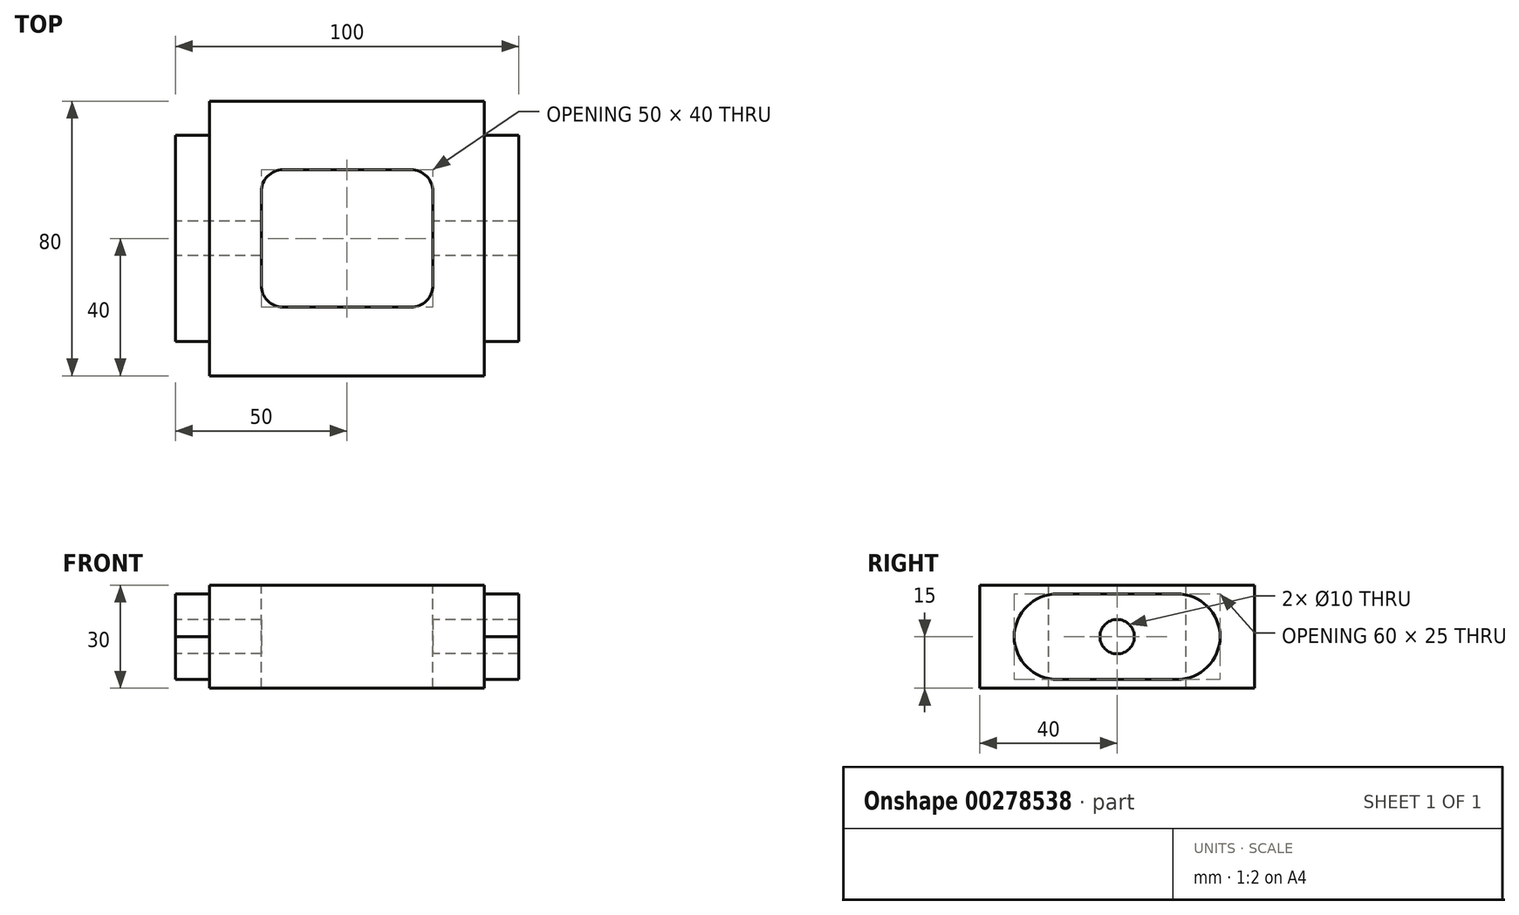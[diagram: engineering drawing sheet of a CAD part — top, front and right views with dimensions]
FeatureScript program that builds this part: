
annotation { "Feature Type Name" : "Feature", "Feature Type Description" : "" }
export const myFeature = defineFeature(function(context is Context, id is Id, definition is map)
    precondition{}
    {
        {
            var Q0;
            Q0=qCreatedBy(makeId("Top.planeOp"),FACE);
            var sketch = newSketch(context, id + "F0", { "sketchPlane" : qUnion([Q0])});
            skLineSegment(sketch, "E0.bottom", {"start": v(40, -40) * mm, "end": v(-40, -40) * mm});
            skLineSegment(sketch, "E0.top", {"start": v(40, 40) * mm, "end": v(-40, 40) * mm});
            skLineSegment(sketch, "E0.left", {"start": v(40, -40) * mm, "end": v(40, 40) * mm});
            skLineSegment(sketch, "E0.right", {"start": v(-40, -40) * mm, "end": v(-40, 40) * mm});
            skPoint(sketch, "E0.middle", {"position": v(0, 0) * mm});
            skSolve(sketch);
        }
        {
            var Q0;
            Q0=makeQuery(id+"F0.imprint","IMPRINT",FACE,{"disambiguationData":[TD([[makeQuery(id+"F0.imprint","IMPRINT",EDGE,{"derivedFrom":sQuery(id+"F0.wireOp",EDGE,"E0.bottom")}),-1.0]])]});
            extrude(context, id + "F1", {"entities" : qUnion([Q0]), "depth" : 30 * mm});
        }
        {
            var Q0;
            Q0=makeQuery(id+"F1.opExtrude","SWEPT_FACE",FACE,{"disambiguationData":[OSD([sQuery(id+"F0.wireOp",EDGE,"E0.right")])]});
            var sketch = newSketch(context, id + "F2", { "sketchPlane" : qUnion([Q0])});
            skLineSegment(sketch, "E1.bottom", {"start": v(30, 27.5) * mm, "end": v(-30, 27.5) * mm});
            skLineSegment(sketch, "E1.top", {"start": v(30, 2.5) * mm, "end": v(-30, 2.5) * mm});
            skLineSegment(sketch, "E1.left", {"start": v(30, 27.5) * mm, "end": v(30, 2.5) * mm});
            skLineSegment(sketch, "E1.right", {"start": v(-30, 27.5) * mm, "end": v(-30, 2.5) * mm});
            skPoint(sketch, "E1.middle", {"position": v(0, 15) * mm});
            skLineSegment(sketch, "E2", {"start": v(-40, 15) * mm, "end": v(40, 15) * mm, "construction": true});
            skSolve(sketch);
        }
        {
            var Q0;
            Q0=makeQuery(id+"F2.imprint","IMPRINT",FACE,{"disambiguationData":[TD([[makeQuery(id+"F2.imprint","IMPRINT",EDGE,{"derivedFrom":sQuery(id+"F2.wireOp",EDGE,"E1.bottom")}),1.0]])]});
            extrude(context, id + "F3", {"entities" : qUnion([Q0]), "operationType" : NewBodyOperationType.ADD, "depth" : 10 * mm});
        }
        {
            var Q0;
            Q0=makeQuery(id+"F1.opExtrude","SWEPT_FACE",FACE,{"disambiguationData":[OSD([sQuery(id+"F0.wireOp",EDGE,"E0.left")])]});
            var sketch = newSketch(context, id + "F4", { "sketchPlane" : qUnion([Q0])});
            skLineSegment(sketch, "E3.bottom", {"start": v(30, 2.5) * mm, "end": v(-30, 2.5) * mm});
            skLineSegment(sketch, "E3.top", {"start": v(30, 27.5) * mm, "end": v(-30, 27.5) * mm});
            skLineSegment(sketch, "E3.left", {"start": v(30, 2.5) * mm, "end": v(30, 27.5) * mm});
            skLineSegment(sketch, "E3.right", {"start": v(-30, 2.5) * mm, "end": v(-30, 27.5) * mm});
            skPoint(sketch, "E3.middle", {"position": v(0, 15) * mm});
            skLineSegment(sketch, "E4", {"start": v(40, 15) * mm, "end": v(-40, 15) * mm, "construction": true});
            skSolve(sketch);
        }
        {
            var Q0;
            Q0=makeQuery(id+"F4.imprint","IMPRINT",FACE,{"disambiguationData":[TD([[makeQuery(id+"F4.imprint","IMPRINT",EDGE,{"derivedFrom":sQuery(id+"F4.wireOp",EDGE,"E3.bottom")}),-1.0]])]});
            extrude(context, id + "F5", {"entities" : qUnion([Q0]), "operationType" : NewBodyOperationType.ADD, "depth" : 10 * mm});
        }
        {
            var Q0;
            Q0=makeQuery(id+"F3.opExtrude","CAP_FACE",FACE,{"disambiguationData":[OSD([sQuery(id+"F2.wireOp",EDGE,"E1.bottom"),sQuery(id+"F2.wireOp",EDGE,"E1.top"),sQuery(id+"F2.wireOp",EDGE,"E1.left"),sQuery(id+"F2.wireOp",EDGE,"E1.right")])],"isStart":false});
            var sketch = newSketch(context, id + "F6", { "sketchPlane" : qUnion([Q0])});
            skCircle(sketch, "E5", {"center": v(0, 15) * mm, "radius": 5 * mm});
            skLineSegment(sketch, "E6", {"start": v(-30, 15) * mm, "end": v(30, 15) * mm, "construction": true});
            skSolve(sketch);
        }
        {
            var Q0;
            Q0 = qSketchRegion(id + "F6", true);
            extrude(context, id + "F7", {"entities" : qUnion([Q0]), "operationType" : NewBodyOperationType.REMOVE, "endBound" : BoundingType.THROUGH_ALL, "oppositeDirection" : true, "depth" : 25 * mm});
        }
        {
            var Q0;
            Q0=makeQuery(id+"F1.opExtrude","CAP_FACE",FACE,{"disambiguationData":[OSD([sQuery(id+"F0.wireOp",EDGE,"E0.bottom"),sQuery(id+"F0.wireOp",EDGE,"E0.top"),sQuery(id+"F0.wireOp",EDGE,"E0.left"),sQuery(id+"F0.wireOp",EDGE,"E0.right")])],"isStart":false});
            var sketch = newSketch(context, id + "F8", { "sketchPlane" : qUnion([Q0])});
            skLineSegment(sketch, "E7.bottom", {"start": v(-25, 20) * mm, "end": v(25, 20) * mm});
            skLineSegment(sketch, "E7.top", {"start": v(-25, -20) * mm, "end": v(25, -20) * mm});
            skLineSegment(sketch, "E7.left", {"start": v(-25, 20) * mm, "end": v(-25, -20) * mm});
            skLineSegment(sketch, "E7.right", {"start": v(25, 20) * mm, "end": v(25, -20) * mm});
            skPoint(sketch, "E7.middle", {"position": v(0, 0) * mm});
            skSolve(sketch);
        }
        {
            var Q0;
            Q0 = qSketchRegion(id + "F8", true);
            extrude(context, id + "F9", {"entities" : qUnion([Q0]), "operationType" : NewBodyOperationType.REMOVE, "endBound" : BoundingType.THROUGH_ALL, "oppositeDirection" : true, "depth" : 25 * mm});
        }
        {
            var Q0;
            Q0=makeQuery(id+"F9.boolean.opBoolean","COPY",EDGE,{"derivedFrom":makeQuery(id+"F9.opExtrude","SWEPT_EDGE",EDGE,{"disambiguationData":[OSD([sQuery(id+"F8.wireOp",EDGE,"E7.bottom"),sQuery(id+"F8.wireOp",EDGE,"E7.left")])]})});
            var Q1;
            Q1=makeQuery(id+"F9.boolean.opBoolean","COPY",EDGE,{"derivedFrom":makeQuery(id+"F9.opExtrude","SWEPT_EDGE",EDGE,{"disambiguationData":[OSD([sQuery(id+"F8.wireOp",EDGE,"E7.bottom"),sQuery(id+"F8.wireOp",EDGE,"E7.right")])]})});
            var Q2;
            Q2=makeQuery(id+"F9.boolean.opBoolean","COPY",EDGE,{"derivedFrom":makeQuery(id+"F9.opExtrude","SWEPT_EDGE",EDGE,{"disambiguationData":[OSD([sQuery(id+"F8.wireOp",EDGE,"E7.top"),sQuery(id+"F8.wireOp",EDGE,"E7.right")])]})});
            var Q3;
            Q3=makeQuery(id+"F9.boolean.opBoolean","COPY",EDGE,{"derivedFrom":makeQuery(id+"F9.opExtrude","SWEPT_EDGE",EDGE,{"disambiguationData":[OSD([sQuery(id+"F8.wireOp",EDGE,"E7.top"),sQuery(id+"F8.wireOp",EDGE,"E7.left")])]})});
            fillet(context, id + "F10", {"entities" : qUnion([Q0, Q1, Q2, Q3]), "radius" : 6.35 * mm, "tangentPropagation" : true, "allowEdgeOverflow" : false});
        }
        {
            var Q0;
            Q0=makeQuery(id+"F5.opExtrude","SWEPT_EDGE",EDGE,{"disambiguationData":[OSD([sQuery(id+"F4.wireOp",EDGE,"E3.top"),sQuery(id+"F4.wireOp",EDGE,"E3.right")])]});
            var Q1;
            Q1=makeQuery(id+"F5.opExtrude","SWEPT_EDGE",EDGE,{"disambiguationData":[OSD([sQuery(id+"F4.wireOp",EDGE,"E3.bottom"),sQuery(id+"F4.wireOp",EDGE,"E3.right")])]});
            var Q2;
            Q2=makeQuery(id+"F5.opExtrude","SWEPT_EDGE",EDGE,{"disambiguationData":[OSD([sQuery(id+"F4.wireOp",EDGE,"E3.bottom"),sQuery(id+"F4.wireOp",EDGE,"E3.left")])]});
            var Q3;
            Q3=makeQuery(id+"F5.opExtrude","SWEPT_EDGE",EDGE,{"disambiguationData":[OSD([sQuery(id+"F4.wireOp",EDGE,"E3.top"),sQuery(id+"F4.wireOp",EDGE,"E3.left")])]});
            var Q4;
            Q4=makeQuery(id+"F3.opExtrude","SWEPT_EDGE",EDGE,{"disambiguationData":[OSD([sQuery(id+"F2.wireOp",EDGE,"E1.top"),sQuery(id+"F2.wireOp",EDGE,"E1.right")])]});
            var Q5;
            Q5=makeQuery(id+"F3.opExtrude","SWEPT_EDGE",EDGE,{"disambiguationData":[OSD([sQuery(id+"F2.wireOp",EDGE,"E1.top"),sQuery(id+"F2.wireOp",EDGE,"E1.left")])]});
            var Q6;
            Q6=makeQuery(id+"F3.opExtrude","SWEPT_EDGE",EDGE,{"disambiguationData":[OSD([sQuery(id+"F2.wireOp",EDGE,"E1.bottom"),sQuery(id+"F2.wireOp",EDGE,"E1.left")])]});
            var Q7;
            Q7=makeQuery(id+"F3.opExtrude","SWEPT_EDGE",EDGE,{"disambiguationData":[OSD([sQuery(id+"F2.wireOp",EDGE,"E1.bottom"),sQuery(id+"F2.wireOp",EDGE,"E1.right")])]});
            fillet(context, id + "F11", {"entities" : qUnion([Q0, Q1, Q2, Q3, Q4, Q5, Q6, Q7]), "radius" : 12.7 * mm, "tangentPropagation" : true, "allowEdgeOverflow" : false});
        }
    });
